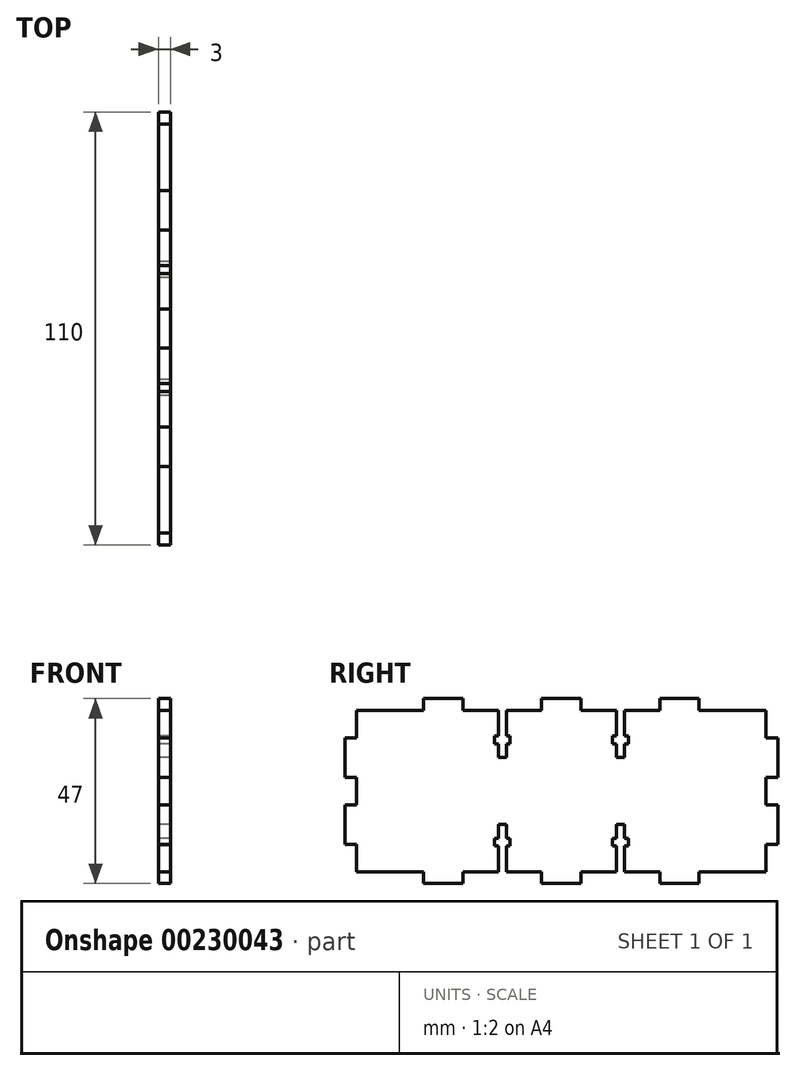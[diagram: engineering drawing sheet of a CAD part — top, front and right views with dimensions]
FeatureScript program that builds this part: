
annotation { "Feature Type Name" : "Feature", "Feature Type Description" : "" }
export const myFeature = defineFeature(function(context is Context, id is Id, definition is map)
    precondition{}
    {
        {
            var Q0;
            Q0=qCreatedBy(makeId("Right.planeOp"),FACE);
            var sketch = newSketch(context, id + "F0", { "sketchPlane" : qUnion([Q0])});
            skLineSegment(sketch, "E0", {"start": v(6.59, 0) * mm, "end": v(6.59, 7) * mm});
            skLineSegment(sketch, "E1", {"start": v(6.59, 7) * mm, "end": v(3.59, 7) * mm});
            skLineSegment(sketch, "E2", {"start": v(3.59, 7) * mm, "end": v(3.59, 17) * mm});
            skLineSegment(sketch, "E3", {"start": v(3.59, 17) * mm, "end": v(6.59, 17) * mm});
            skLineSegment(sketch, "E4", {"start": v(6.59, 17) * mm, "end": v(6.59, 24) * mm});
            skLineSegment(sketch, "E5", {"start": v(6.59, 24) * mm, "end": v(3.59, 24) * mm});
            skLineSegment(sketch, "E6", {"start": v(3.59, 24) * mm, "end": v(3.59, 34) * mm});
            skLineSegment(sketch, "E7", {"start": v(3.59, 34) * mm, "end": v(6.59, 34) * mm});
            skLineSegment(sketch, "E8", {"start": v(6.59, 34) * mm, "end": v(6.59, 41) * mm});
            skLineSegment(sketch, "E9", {"start": v(6.59, 41) * mm, "end": v(23.59, 41) * mm});
            skLineSegment(sketch, "E10", {"start": v(23.59, 41) * mm, "end": v(23.59, 44) * mm});
            skLineSegment(sketch, "E11", {"start": v(23.59, 44) * mm, "end": v(33.59, 44) * mm});
            skLineSegment(sketch, "E12", {"start": v(33.59, 44) * mm, "end": v(33.59, 41) * mm});
            skLineSegment(sketch, "E13", {"start": v(33.59, 41) * mm, "end": v(42.59, 41) * mm});
            skLineSegment(sketch, "E14", {"start": v(53.59, 41) * mm, "end": v(53.59, 44) * mm});
            skLineSegment(sketch, "E15", {"start": v(53.59, 44) * mm, "end": v(58.59, 44) * mm});
            skLineSegment(sketch, "E16", {"start": v(6.59, 20.5) * mm, "end": v(58.59, 20.5) * mm, "construction": true});
            skLineSegment(sketch, "E17", {"start": v(58.59, 44) * mm, "end": v(58.59, 0) * mm, "construction": true});
            skLineSegment(sketch, "E18.MirrorCS", {"start": v(53.59, -3) * mm, "end": v(58.59, -3) * mm});
            skLineSegment(sketch, "E19.MirrorCS", {"start": v(53.59, 0) * mm, "end": v(53.59, -3) * mm});
            skLineSegment(sketch, "E20.MirrorCS", {"start": v(33.59, -3) * mm, "end": v(33.59, 0) * mm});
            skLineSegment(sketch, "E21.MirrorCS", {"start": v(3.59, 7) * mm, "end": v(6.59, 7) * mm});
            skLineSegment(sketch, "E22.MirrorCS", {"start": v(6.59, 17) * mm, "end": v(3.59, 17) * mm});
            skLineSegment(sketch, "E23.MirrorCS", {"start": v(23.59, 0) * mm, "end": v(23.59, -3) * mm});
            skLineSegment(sketch, "E24.MirrorCS", {"start": v(33.59, 0) * mm, "end": v(42.59, 0) * mm});
            skLineSegment(sketch, "E25.MirrorCS", {"start": v(23.59, -3) * mm, "end": v(33.59, -3) * mm});
            skLineSegment(sketch, "E26.MirrorCS", {"start": v(3.59, 17) * mm, "end": v(3.59, 7) * mm});
            skLineSegment(sketch, "E27.MirrorCS", {"start": v(6.59, 7) * mm, "end": v(6.59, 0) * mm});
            skLineSegment(sketch, "E28.MirrorCS", {"start": v(6.59, 0) * mm, "end": v(23.59, 0) * mm});
            skLineSegment(sketch, "E29.MirrorCS", {"start": v(113.59, 7) * mm, "end": v(110.59, 7) * mm});
            skLineSegment(sketch, "E30.MirrorCS", {"start": v(113.59, 17) * mm, "end": v(110.59, 17) * mm});
            skLineSegment(sketch, "E31.MirrorCS", {"start": v(110.59, 17) * mm, "end": v(113.59, 17) * mm});
            skLineSegment(sketch, "E32.MirrorCS", {"start": v(110.59, 7) * mm, "end": v(113.59, 7) * mm});
            skLineSegment(sketch, "E33.MirrorCS", {"start": v(83.59, -3) * mm, "end": v(83.59, 0) * mm});
            skLineSegment(sketch, "E34.MirrorCS", {"start": v(93.59, 0) * mm, "end": v(93.59, -3) * mm});
            skLineSegment(sketch, "E35.MirrorCS", {"start": v(83.59, 44) * mm, "end": v(83.59, 41) * mm});
            skLineSegment(sketch, "E36.MirrorCS", {"start": v(93.59, 41) * mm, "end": v(93.59, 44) * mm});
            skLineSegment(sketch, "E37.MirrorCS", {"start": v(113.59, 34) * mm, "end": v(110.59, 34) * mm});
            skLineSegment(sketch, "E38.MirrorCS", {"start": v(110.59, 24) * mm, "end": v(113.59, 24) * mm});
            skLineSegment(sketch, "E39.MirrorCS", {"start": v(63.59, 41) * mm, "end": v(63.59, 44) * mm});
            skLineSegment(sketch, "E40.MirrorCS", {"start": v(63.59, 0) * mm, "end": v(63.59, -3) * mm});
            skLineSegment(sketch, "E41.MirrorCS", {"start": v(110.59, 0) * mm, "end": v(110.59, 7) * mm});
            skLineSegment(sketch, "E42.MirrorCS", {"start": v(110.59, 17) * mm, "end": v(110.59, 24) * mm});
            skLineSegment(sketch, "E43.MirrorCS", {"start": v(113.59, 17) * mm, "end": v(113.59, 7) * mm});
            skLineSegment(sketch, "E44.MirrorCS", {"start": v(110.59, 20.5) * mm, "end": v(58.59, 20.5) * mm, "construction": true});
            skLineSegment(sketch, "E45.MirrorCS", {"start": v(63.59, -3) * mm, "end": v(58.59, -3) * mm});
            skLineSegment(sketch, "E46.MirrorCS", {"start": v(93.59, -3) * mm, "end": v(83.59, -3) * mm});
            skLineSegment(sketch, "E47.MirrorCS", {"start": v(110.59, 7) * mm, "end": v(110.59, 0) * mm});
            skLineSegment(sketch, "E48.MirrorCS", {"start": v(93.59, 44) * mm, "end": v(83.59, 44) * mm});
            skLineSegment(sketch, "E49.MirrorCS", {"start": v(110.59, 41) * mm, "end": v(93.59, 41) * mm});
            skLineSegment(sketch, "E50.MirrorCS", {"start": v(110.59, 34) * mm, "end": v(110.59, 41) * mm});
            skLineSegment(sketch, "E51.MirrorCS", {"start": v(113.59, 24) * mm, "end": v(113.59, 34) * mm});
            skLineSegment(sketch, "E52.MirrorCS", {"start": v(63.59, 44) * mm, "end": v(58.59, 44) * mm});
            skLineSegment(sketch, "E53.MirrorCS", {"start": v(83.59, 41) * mm, "end": v(74.59, 41) * mm});
            skLineSegment(sketch, "E54.MirrorCS", {"start": v(113.59, 7) * mm, "end": v(113.59, 17) * mm});
            skLineSegment(sketch, "E55.MirrorCS", {"start": v(83.59, 0) * mm, "end": v(74.59, 0) * mm});
            skLineSegment(sketch, "E56.MirrorCS", {"start": v(110.59, 0) * mm, "end": v(93.59, 0) * mm});
            skLineSegment(sketch, "E57.top", {"start": v(42.59, 29) * mm, "end": v(44.59, 29) * mm});
            skLineSegment(sketch, "E57.left", {"start": v(42.59, 41) * mm, "end": v(42.59, 34.5) * mm});
            skLineSegment(sketch, "E57.right", {"start": v(44.59, 41) * mm, "end": v(44.59, 34.5) * mm});
            skLineSegment(sketch, "E58.bottom", {"start": v(41.59, 34.5) * mm, "end": v(42.59, 34.5) * mm});
            skLineSegment(sketch, "E58.top", {"start": v(41.59, 32.5) * mm, "end": v(42.59, 32.5) * mm});
            skLineSegment(sketch, "E58.left", {"start": v(41.59, 34.5) * mm, "end": v(41.59, 32.5) * mm});
            skLineSegment(sketch, "E58.right", {"start": v(45.59, 34.5) * mm, "end": v(45.59, 32.5) * mm});
            skLineSegment(sketch, "E59.trimOffspring", {"start": v(44.59, 41) * mm, "end": v(53.59, 41) * mm});
            skLineSegment(sketch, "E60.trimOffspring", {"start": v(42.59, 32.5) * mm, "end": v(42.59, 29) * mm});
            skLineSegment(sketch, "E61.trimOffspring", {"start": v(44.59, 34.5) * mm, "end": v(45.59, 34.5) * mm});
            skLineSegment(sketch, "E62.trimOffspring", {"start": v(44.59, 32.5) * mm, "end": v(44.59, 29) * mm});
            skLineSegment(sketch, "E63.trimOffspring", {"start": v(44.59, 32.5) * mm, "end": v(45.59, 32.5) * mm});
            skLineSegment(sketch, "E64.MirrorCS", {"start": v(44.59, 6.5) * mm, "end": v(45.59, 6.5) * mm});
            skLineSegment(sketch, "E65.MirrorCS", {"start": v(44.59, 0) * mm, "end": v(44.59, 6.5) * mm});
            skLineSegment(sketch, "E66.MirrorCS", {"start": v(41.59, 6.5) * mm, "end": v(42.59, 6.5) * mm});
            skLineSegment(sketch, "E67.MirrorCS", {"start": v(41.59, 6.5) * mm, "end": v(41.59, 8.5) * mm});
            skLineSegment(sketch, "E68.MirrorCS", {"start": v(41.59, 8.5) * mm, "end": v(42.59, 8.5) * mm});
            skLineSegment(sketch, "E69.MirrorCS", {"start": v(44.59, 8.5) * mm, "end": v(45.59, 8.5) * mm});
            skLineSegment(sketch, "E70.MirrorCS", {"start": v(44.59, 8.5) * mm, "end": v(44.59, 12) * mm});
            skLineSegment(sketch, "E71.MirrorCS", {"start": v(42.59, 12) * mm, "end": v(44.59, 12) * mm});
            skLineSegment(sketch, "E72.MirrorCS", {"start": v(42.59, 0) * mm, "end": v(42.59, 6.5) * mm});
            skLineSegment(sketch, "E73.MirrorCS", {"start": v(42.59, 8.5) * mm, "end": v(42.59, 12) * mm});
            skLineSegment(sketch, "E74.MirrorCS", {"start": v(45.59, 6.5) * mm, "end": v(45.59, 8.5) * mm});
            skLineSegment(sketch, "E75.MirrorCS", {"start": v(75.59, 34.5) * mm, "end": v(74.59, 34.5) * mm});
            skLineSegment(sketch, "E76.MirrorCS", {"start": v(74.59, 12) * mm, "end": v(72.59, 12) * mm});
            skLineSegment(sketch, "E77.MirrorCS", {"start": v(75.59, 34.5) * mm, "end": v(75.59, 32.5) * mm});
            skLineSegment(sketch, "E78.MirrorCS", {"start": v(72.59, 6.5) * mm, "end": v(71.59, 6.5) * mm});
            skLineSegment(sketch, "E79.MirrorCS", {"start": v(72.59, 8.5) * mm, "end": v(71.59, 8.5) * mm});
            skLineSegment(sketch, "E80.MirrorCS", {"start": v(75.59, 32.5) * mm, "end": v(74.59, 32.5) * mm});
            skLineSegment(sketch, "E81.MirrorCS", {"start": v(72.59, 32.5) * mm, "end": v(71.59, 32.5) * mm});
            skLineSegment(sketch, "E82.MirrorCS", {"start": v(75.59, 6.5) * mm, "end": v(74.59, 6.5) * mm});
            skLineSegment(sketch, "E83.MirrorCS", {"start": v(75.59, 8.5) * mm, "end": v(74.59, 8.5) * mm});
            skLineSegment(sketch, "E84.MirrorCS", {"start": v(74.59, 29) * mm, "end": v(72.59, 29) * mm});
            skLineSegment(sketch, "E85.MirrorCS", {"start": v(71.59, 6.5) * mm, "end": v(71.59, 8.5) * mm});
            skLineSegment(sketch, "E86.MirrorCS", {"start": v(71.59, 34.5) * mm, "end": v(71.59, 32.5) * mm});
            skLineSegment(sketch, "E87.MirrorCS", {"start": v(72.59, 34.5) * mm, "end": v(71.59, 34.5) * mm});
            skLineSegment(sketch, "E88.MirrorCS", {"start": v(75.59, 6.5) * mm, "end": v(75.59, 8.5) * mm});
            skLineSegment(sketch, "E89.MirrorCS", {"start": v(74.59, 41) * mm, "end": v(74.59, 34.5) * mm});
            skLineSegment(sketch, "E90.MirrorCS", {"start": v(74.59, 8.5) * mm, "end": v(74.59, 12) * mm});
            skLineSegment(sketch, "E91.MirrorCS", {"start": v(72.59, 8.5) * mm, "end": v(72.59, 12) * mm});
            skLineSegment(sketch, "E92.MirrorCS", {"start": v(72.59, 41) * mm, "end": v(72.59, 34.5) * mm});
            skLineSegment(sketch, "E93.MirrorCS", {"start": v(74.59, 32.5) * mm, "end": v(74.59, 29) * mm});
            skLineSegment(sketch, "E94.MirrorCS", {"start": v(72.59, 32.5) * mm, "end": v(72.59, 29) * mm});
            skLineSegment(sketch, "E95.MirrorCS", {"start": v(74.59, 0) * mm, "end": v(74.59, 6.5) * mm});
            skLineSegment(sketch, "E96.MirrorCS", {"start": v(72.59, 0) * mm, "end": v(72.59, 6.5) * mm});
            skLineSegment(sketch, "E97.trimOffspring", {"start": v(72.59, 41) * mm, "end": v(63.59, 41) * mm});
            skLineSegment(sketch, "E98.trimOffspring", {"start": v(72.59, 0) * mm, "end": v(63.59, 0) * mm});
            skLineSegment(sketch, "E99.trimOffspring", {"start": v(44.59, 0) * mm, "end": v(53.59, 0) * mm});
            skSolve(sketch);
        }
        {
            var Q0;
            Q0=makeQuery(id+"F0.imprint","IMPRINT",FACE,{"disambiguationData":[TD([[makeQuery(id+"F0.imprint","IMPRINT",EDGE,{"derivedFrom":sQuery(id+"F0.wireOp",EDGE,"E4")}),-1.0]])]});
            extrude(context, id + "F1", {"entities" : qUnion([Q0]), "depth" : 3 * mm});
        }
    });
